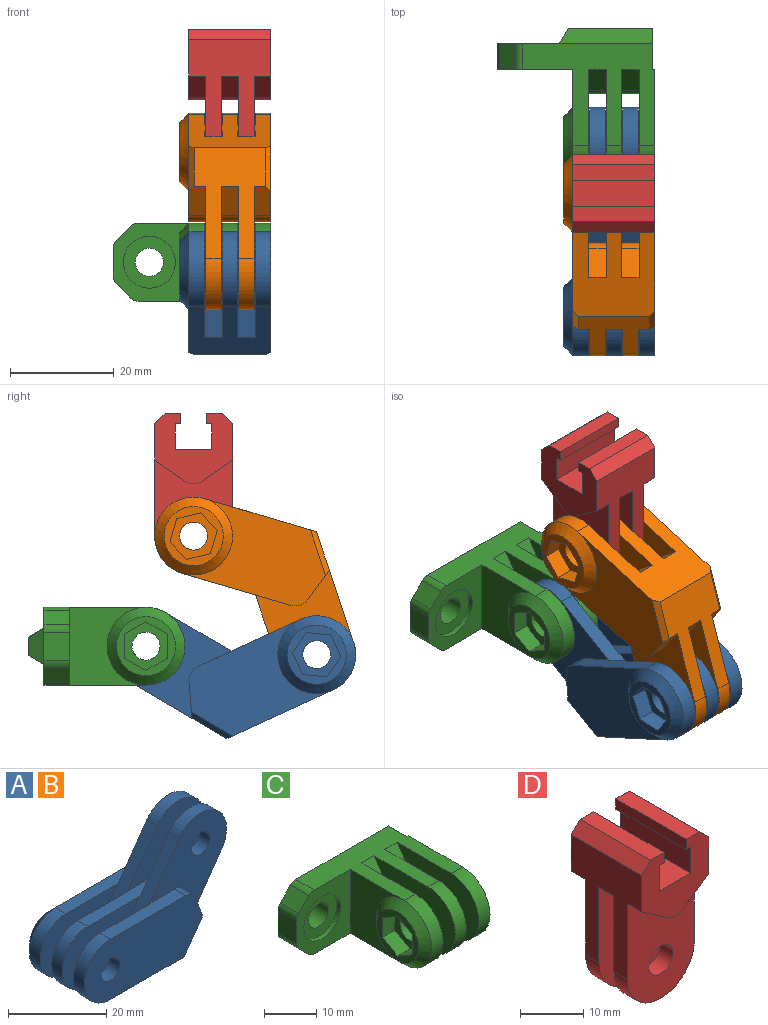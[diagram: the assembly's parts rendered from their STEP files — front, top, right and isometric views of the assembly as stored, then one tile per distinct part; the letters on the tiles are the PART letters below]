
ASSEMBLY  parts=4 mates=4
PART A: 48 faces, bbox 44.2x17.6x30.2 mm
  f0: plane 21.71x3.36mm, normal (0,0,1), area 67.1mm2, adj f4,f6,f11,f13,f20,f25,f26,f31
  f1: plane 26.52x15mm, normal (0,1,0), area 278.6mm2, adj f2,f16,f21,f22,f36,f46
  f2: plane 21.71x3.26mm, normal (0,0,1), area 67.8mm2, adj f1,f3,f4,f21,f28,f29
  f3: plane 23.8x22.05mm, normal (0,1,0), area 246.6mm2, adj f2,f4,f5,f7,f16,f17,f21
  f4: plane 17.78x12.45mm, normal (-0.82,0,0.57), area 67.1mm2, adj f0,f2,f3,f5,f6,f25,f28,f45
  f5: cylinder r=7.5mm len=13.64mm, axis (0,-1,0), area 69.7mm2, adj f3,f4,f6,f17
  f6: plane 23.8x22.05mm, normal (0,-1,0), area 246.6mm2, adj f0,f4,f5,f7,f15,f17,f20
  f7: cylinder r=2.7mm len=5.4mm, axis (0,-1,0), area 50.2mm2, adj f3,f6
  f8: plane 34.02x15mm, normal (0,-1,0), area 432.4mm2, adj f9,f18,f19,f22,f33,f34,f47
  f9: plane 21.71x3.26mm, normal (0,0,1), area 67.8mm2, adj f8,f10,f11,f19,f32,f33
  f10: plane 23.8x22.05mm, normal (0,-1,0), area 246.6mm2, adj f9,f11,f12,f14,f17,f18,f19
  f11: plane 17.78x12.45mm, normal (-0.82,0,0.57), area 67.1mm2, adj f0,f9,f10,f12,f13,f31,f32,f44
  f12: cylinder r=7.5mm len=13.64mm, axis (0,1,0), area 69.7mm2, adj f10,f11,f13,f17
  f13: plane 23.8x22.05mm, normal (0,1,0), area 246.6mm2, adj f0,f11,f12,f14,f15,f17,f20
  f14: cylinder r=2.7mm len=5.4mm, axis (0,1,0), area 50.2mm2, adj f10,f13
  f15: plane 6.63x3.36mm, normal (0.94,0,0.34), area 23.7mm2, adj f6,f13,f17,f20
  f16: plane 6.63x3.26mm, normal (0.94,0,0.34), area 22.4mm2, adj f1,f3,f17,f21,f46
  f17: plane 18.4x13.8mm, normal (0.82,0,-0.57), area 194.5mm2, adj f3,f5,f6,f10,f12,f13,f15,f16
  f18: plane 6.63x3.26mm, normal (0.94,0,0.34), area 22.4mm2, adj f8,f10,f17,f19,f47
  f19: cylinder r=3mm len=3.26mm, axis (0,1,0), area 11.9mm2, adj f8,f9,f10,f18
  f20: cylinder r=3mm len=3.36mm, axis (0,-1,0), area 12.3mm2, adj f0,f6,f13,f15
  f21: cylinder r=3mm len=3.26mm, axis (0,-1,0), area 11.9mm2, adj f1,f2,f3,f16
  f22: plane 22.46x15.8mm, normal (0,0,-1), area 255.2mm2, adj f1,f8,f17,f24,f25,f26,f28,f29
  f23: cylinder r=2.7mm len=5.4mm, axis (0,-1,0), area 25.4mm2, adj f28,f37
  f24: plane 5.78x4.05mm, normal (-0.82,0,-0.57), area 23.7mm2, adj f22,f25,f28,f45
  f25: plane 22.15x15mm, normal (0,1,0), area 246.6mm2, adj f0,f4,f22,f24,f26,f27,f45
  f26: cylinder r=7.5mm len=15mm, axis (0,-1,0), area 69.7mm2, adj f0,f22,f25,f31
  f27: cylinder r=2.7mm len=5.4mm, axis (0,-1,0), area 50.2mm2, adj f25,f31
  f28: plane 22.15x15mm, normal (0,-1,0), area 246.6mm2, adj f2,f4,f22,f23,f24,f29,f45
  f29: cylinder r=7.5mm len=15mm, axis (0,-1,0), area 72.1mm2, adj f2,f22,f28,f36
  f30: plane 5.78x4.05mm, normal (-0.82,0,-0.57), area 23.7mm2, adj f22,f31,f32,f44
  f31: plane 22.15x15mm, normal (0,-1,0), area 246.6mm2, adj f0,f11,f22,f26,f27,f30,f44
  f32: plane 22.15x15mm, normal (0,1,0), area 246.6mm2, adj f9,f11,f22,f30,f33,f34,f44
  f33: cylinder r=7.5mm len=15mm, axis (0,1,0), area 72.1mm2, adj f8,f9,f22,f32
  f34: cylinder r=2.7mm len=5.4mm, axis (0,1,0), area 51.9mm2, adj f8,f32
  f35: plane 11.4x11.4mm, normal (0,1,0), area 45.3mm2, adj f36,f38,f39,f40,f41,f42,f43
  f36: cone r=5.7mm half-angle=45deg, axis (0,-1,0), area 105.6mm2, adj f1,f29,f35
  f37: plane 9.35x8.1mm, normal (0,1,0), area 33.9mm2, adj f23,f38,f39,f40,f41,f42,f43
  f38: plane 4.68x3.36mm, normal (1,0,0), area 15.7mm2, adj f35,f37,f39,f43
  f39: plane 4.05x3.36mm, normal (0.5,0,-0.87), area 15.7mm2, adj f35,f37,f38,f40
  f40: plane 4.05x3.36mm, normal (-0.5,0,-0.87), area 15.7mm2, adj f35,f37,f39,f41
  f41: plane 4.68x3.36mm, normal (-1,0,0), area 15.7mm2, adj f35,f37,f40,f42
  f42: plane 4.05x3.36mm, normal (-0.5,0,0.87), area 15.7mm2, adj f35,f37,f41,f43
  f43: plane 4.05x3.36mm, normal (0.5,0,0.87), area 15.7mm2, adj f35,f37,f38,f42
  f44: cylinder r=3mm len=3.44mm, axis (0,1,0), area 12.3mm2, adj f11,f30,f31,f32
  f45: cylinder r=3mm len=3.44mm, axis (0,-1,0), area 12.3mm2, adj f4,f24,f25,f28
  f46: plane 7.54x5.7mm, normal (0.58,0.71,-0.41), area 12mm2, adj f1,f16,f17,f22
  f47: plane 7.54x5.7mm, normal (0.58,-0.71,-0.41), area 12mm2, adj f8,f17,f18,f22
PART B: same geometry as A
PART C: 47 faces, bbox 30.4x30.2x15 mm
  f0: cylinder r=2.7mm len=5.4mm, axis (0,-1,0), area 67.9mm2, adj f6,f17
  f1: plane 25.57x19.65mm, normal (0,0,-1), area 258.9mm2, adj f2,f5,f6,f16,f19,f21,f22,f23
  f2: plane 15x8mm, normal (1,0,0), area 90.8mm2, adj f1,f3,f6,f7,f8,f10,f19
  f3: plane 25.57x19.65mm, normal (0,0,1), area 258.9mm2, adj f2,f5,f6,f13,f19,f22,f23,f24
  f4: plane 5.34x5mm, normal (-1,0,0), area 26.7mm2, adj f5,f6,f14,f15
  f5: plane 15x14.6mm, normal (0,-1,0), area 124.1mm2, adj f1,f3,f4,f11,f12,f13,f14,f15
  f6: plane 30x15mm, normal (0,1,0), area 284.8mm2, adj f0,f1,f2,f3,f4,f7,f8,f9
  f7: plane 18x3mm, normal (0,0.5,0.87), area 59.4mm2, adj f2,f6,f9,f10
  f8: plane 18x3mm, normal (0,0.5,-0.87), area 59.4mm2, adj f2,f6,f9,f10
  f9: plane 7x3mm, normal (-0.87,0.5,0), area 18.2mm2, adj f6,f7,f8,f10
  f10: plane 16.27x3.54mm, normal (0,1,0), area 57.5mm2, adj f2,f7,f8,f9
  f11: plane 5x2.83mm, normal (-0.71,0,-0.71), area 20mm2, adj f5,f6,f14,f16
  f12: plane 5x2.83mm, normal (-0.71,0,0.71), area 20mm2, adj f5,f6,f13,f15
  f13: cylinder r=2mm len=5mm, axis (0,1,0), area 7.9mm2, adj f3,f5,f6,f12
  f14: cylinder r=2mm len=5mm, axis (0,1,0), area 7.9mm2, adj f4,f5,f6,f11
  f15: cylinder r=2mm len=5mm, axis (0,1,0), area 7.9mm2, adj f4,f5,f6,f12
  f16: cylinder r=2mm len=5mm, axis (0,-1,0), area 7.9mm2, adj f1,f5,f6,f11
  f17: plane 10x10mm, normal (0,-1,0), area 55.6mm2, adj f0,f18
  f18: cylinder r=5mm len=10mm, axis (0,-1,0), area 31.4mm2, adj f5,f17
  f19: plane 15x0.4mm, normal (0,1,0), area 6mm2, adj f1,f2,f3,f29
  f20: cylinder r=2.7mm len=5.4mm, axis (1,0,0), area 25.4mm2, adj f26,f38
  f21: plane 5.78x4.05mm, normal (0,-0.82,-0.57), area 23.7mm2, adj f1,f23,f26,f46
  f22: plane 15x14.65mm, normal (-1,0,0), area 131.4mm2, adj f1,f3,f5,f37
  f23: plane 22.15x15mm, normal (-1,0,0), area 246.6mm2, adj f1,f3,f21,f24,f25,f34,f46
  f24: cylinder r=7.5mm len=15mm, axis (1,0,0), area 69.7mm2, adj f1,f3,f23,f30
  f25: cylinder r=2.7mm len=5.4mm, axis (1,0,0), area 50.2mm2, adj f23,f30
  f26: plane 22.15x15mm, normal (1,0,0), area 246.6mm2, adj f1,f3,f20,f21,f27,f34,f46
  f27: cylinder r=7.5mm len=15mm, axis (1,0,0), area 72.1mm2, adj f1,f3,f26,f37
  f28: plane 5.78x4.05mm, normal (0,-0.82,-0.57), area 23.7mm2, adj f1,f30,f31,f45
  f29: plane 22.15x15mm, normal (1,0,0), area 285.2mm2, adj f1,f3,f19,f32,f33
  f30: plane 22.15x15mm, normal (1,0,0), area 246.6mm2, adj f1,f3,f24,f25,f28,f35,f45
  f31: plane 22.15x15mm, normal (-1,0,0), area 246.6mm2, adj f1,f3,f28,f32,f33,f35,f45
  f32: cylinder r=7.5mm len=15mm, axis (-1,0,0), area 72.1mm2, adj f1,f3,f29,f31
  f33: cylinder r=2.7mm len=5.4mm, axis (-1,0,0), area 51.9mm2, adj f29,f31
  f34: plane 5.78x4.05mm, normal (0,-0.82,0.57), area 23.7mm2, adj f3,f23,f26,f46
  f35: plane 5.78x4.05mm, normal (0,-0.82,0.57), area 23.7mm2, adj f3,f30,f31,f45
  f36: plane 11.4x11.4mm, normal (-1,0,0), area 45.3mm2, adj f37,f39,f40,f41,f42,f43,f44
  f37: cone r=5.7mm half-angle=45deg, axis (1,0,0), area 105.6mm2, adj f22,f27,f36
  f38: plane 9.35x8.1mm, normal (-1,0,0), area 33.9mm2, adj f20,f39,f40,f41,f42,f43,f44
  f39: plane 4.68x3.36mm, normal (0,1,0), area 15.7mm2, adj f36,f38,f40,f44
  f40: plane 4.05x3.36mm, normal (0,0.5,-0.87), area 15.7mm2, adj f36,f38,f39,f41
  f41: plane 4.05x3.36mm, normal (0,-0.5,-0.87), area 15.7mm2, adj f36,f38,f40,f42
  f42: plane 4.68x3.36mm, normal (0,-1,0), area 15.7mm2, adj f36,f38,f41,f43
  f43: plane 4.05x3.36mm, normal (0,-0.5,0.87), area 15.7mm2, adj f36,f38,f42,f44
  f44: plane 4.05x3.36mm, normal (0,0.5,0.87), area 15.7mm2, adj f36,f38,f39,f43
  f45: cylinder r=3mm len=3.44mm, axis (-1,0,0), area 12.3mm2, adj f28,f30,f31,f35
  f46: cylinder r=3mm len=3.44mm, axis (1,0,0), area 12.3mm2, adj f21,f23,f26,f34
PART D: 32 faces, bbox 15x15.8x31.2 mm
  f0: plane 15.8x7mm, normal (0,0,1), area 110.6mm2, adj f1,f6,f7,f8
  f1: plane 15.8x5mm, normal (1,0,0), area 79mm2, adj f0,f2,f6,f7
  f2: plane 15.8x1mm, normal (0,0,-1), area 15.8mm2, adj f1,f3,f6,f7
  f3: plane 15.8x2mm, normal (1,0,0), area 31.6mm2, adj f2,f4,f6,f7
  f4: plane 15.8x3mm, normal (0,0,1), area 47.4mm2, adj f3,f6,f7,f14
  f5: plane 21.65x15.8mm, normal (-1,0,0), area 197.3mm2, adj f6,f7,f14,f15,f16,f17,f18,f19
  f6: plane 15x13.59mm, normal (0,-1,0), area 124.6mm2, adj f0,f1,f2,f3,f4,f5,f8,f9
  f7: plane 15x13.59mm, normal (0,1,0), area 124.6mm2, adj f0,f1,f2,f3,f4,f5,f8,f9
  f8: plane 15.8x5mm, normal (-1,0,0), area 79mm2, adj f0,f6,f7,f9
  f9: plane 15.8x1mm, normal (0,0,-1), area 15.8mm2, adj f6,f7,f8,f10
  f10: plane 15.8x2mm, normal (-1,0,0), area 31.6mm2, adj f6,f7,f9,f11
  f11: plane 15.8x3mm, normal (0,0,1), area 47.4mm2, adj f6,f7,f10,f13
  f12: plane 21.65x15.8mm, normal (1,0,0), area 197.3mm2, adj f6,f7,f13,f17,f18,f19,f22,f23
  f13: plane 15.8x2mm, normal (0.71,0,0.71), area 44.7mm2, adj f6,f7,f11,f12
  f14: plane 15.8x2mm, normal (-0.71,0,0.71), area 44.7mm2, adj f4,f5,f6,f7
  f15: plane 5.78x4.05mm, normal (-0.57,0,-0.82), area 23.7mm2, adj f5,f19,f24,f30
  f16: plane 5.78x4.05mm, normal (-0.57,0,-0.82), area 23mm2, adj f5,f6,f17,f31
  f17: plane 22.15x15mm, normal (0,-1,0), area 246.6mm2, adj f5,f12,f16,f18,f20,f27,f31
  f18: cylinder r=7.5mm len=15mm, axis (0,1,0), area 69.7mm2, adj f5,f12,f17,f19
  f19: plane 22.15x15mm, normal (0,1,0), area 246.6mm2, adj f5,f12,f15,f18,f20,f26,f30
  f20: cylinder r=2.7mm len=5.4mm, axis (0,1,0), area 50.2mm2, adj f17,f19
  f21: plane 5.78x4.05mm, normal (-0.57,0,-0.82), area 23mm2, adj f5,f7,f22,f29
  f22: plane 22.15x15mm, normal (0,1,0), area 246.6mm2, adj f5,f12,f21,f23,f25,f28,f29
  f23: cylinder r=7.5mm len=15mm, axis (0,-1,0), area 69.7mm2, adj f5,f12,f22,f24
  f24: plane 22.15x15mm, normal (0,-1,0), area 246.6mm2, adj f5,f12,f15,f23,f25,f26,f30
  f25: cylinder r=2.7mm len=5.4mm, axis (0,-1,0), area 50.2mm2, adj f22,f24
  f26: plane 5.78x4.05mm, normal (0.57,0,-0.82), area 23.7mm2, adj f12,f19,f24,f30
  f27: plane 5.78x4.05mm, normal (0.57,0,-0.82), area 23mm2, adj f6,f12,f17,f31
  f28: plane 5.78x4.05mm, normal (0.57,0,-0.82), area 23mm2, adj f7,f12,f22,f29
  f29: cylinder r=3mm len=3.44mm, axis (0,-1,0), area 11.9mm2, adj f7,f21,f22,f28
  f30: cylinder r=3mm len=3.44mm, axis (0,1,0), area 12.3mm2, adj f15,f19,f24,f26
  f31: cylinder r=3mm len=3.44mm, axis (0,1,0), area 11.9mm2, adj f6,f16,f17,f27
PLACE A rot(axis=(-0.21,0.21,0.96),92.6deg) t=(-20.44,-38.01,1.49)mm
PLACE B rot(axis=(-0.7,0.7,0.1),168.4deg) t=(-20.44,-41.68,26.29)mm
PLACE C t=(-12.94,1.2,1.73)mm fixed
PLACE D rot(axis=(0,0,1),90deg) t=(-28.34,-27.62,45.09)mm
MATE revolute B.f5 <-> A.f23  axis (-1,0,0) through (-25.08,-51.33,7.6)mm
MATE revolute B.f23 <-> D.f18  axis (1,0,0) through (-25.28,-27.62,30.43)mm
MATE parallel D.f0 <-> C.f3  axis (0,0,1) through (-20.44,-27.62,47.09)mm
MATE revolute A.f5 <-> C.f20  axis (-1,0,0) through (-25.08,-18.45,9.23)mm
